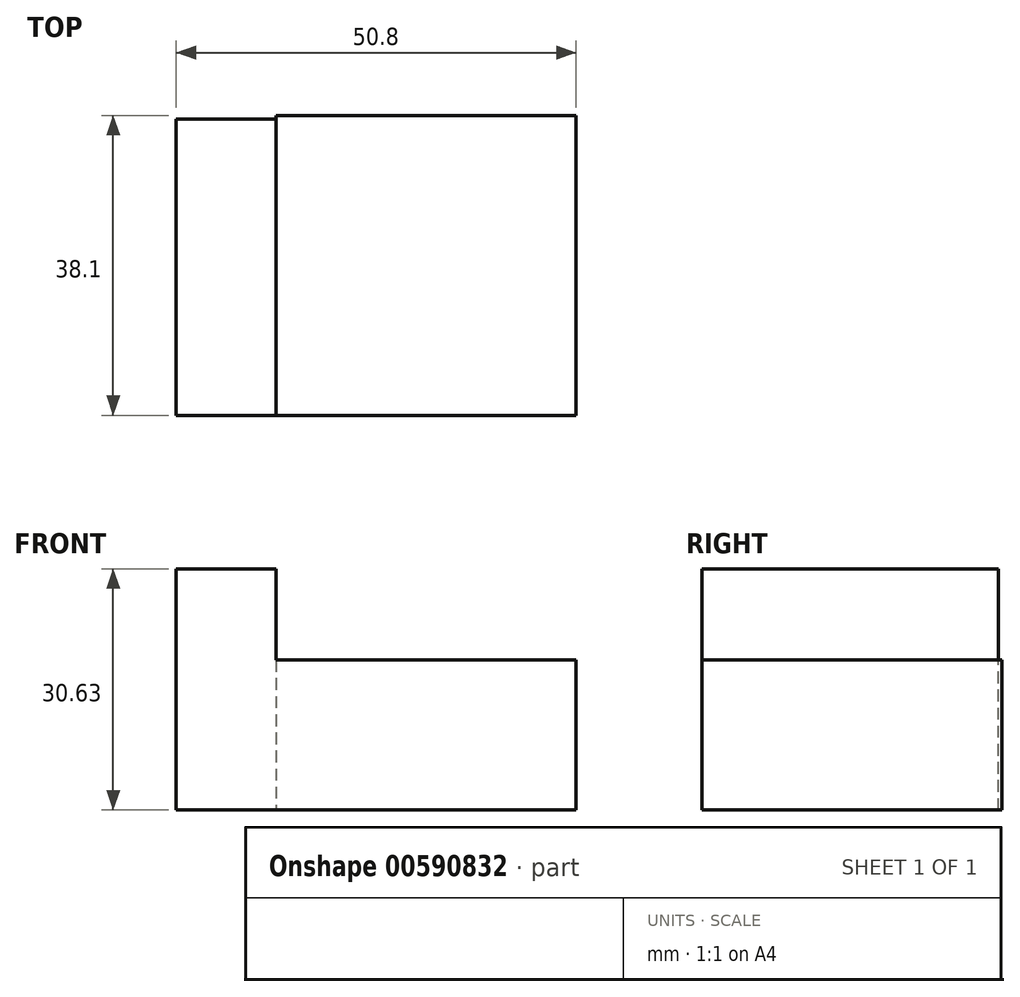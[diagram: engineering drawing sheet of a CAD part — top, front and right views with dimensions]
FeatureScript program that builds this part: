
annotation { "Feature Type Name" : "Feature", "Feature Type Description" : "" }
export const myFeature = defineFeature(function(context is Context, id is Id, definition is map)
    precondition{}
    {
        {
            var Q0;
            Q0=qCreatedBy(makeId("Top.planeOp"),FACE);
            var sketch = newSketch(context, id + "F0", { "sketchPlane" : qUnion([Q0])});
            skLineSegment(sketch, "E0", {"start": v(-21.24, 17.91) * mm, "end": v(-21.24, -20.19) * mm});
            skLineSegment(sketch, "E1", {"start": v(-21.24, -20.19) * mm, "end": v(16.86, -20.19) * mm});
            skLineSegment(sketch, "E2", {"start": v(16.86, -20.19) * mm, "end": v(16.86, 17.91) * mm});
            skLineSegment(sketch, "E3", {"start": v(16.86, 17.91) * mm, "end": v(-21.24, 17.91) * mm});
            skSolve(sketch);
        }
        {
            var Q0;
            Q0=makeQuery(id+"F0.imprint","IMPRINT",FACE,{"disambiguationData":[TD([[makeQuery(id+"F0.imprint","IMPRINT",EDGE,{"derivedFrom":sQuery(id+"F0.wireOp",EDGE,"E0")}),1.0]])]});
            extrude(context, id + "F1", {"entities" : qUnion([Q0]), "depth" : 19.05 * mm, "offsetDistance" : 25.4 * mm});
        }
        {
            var Q0;
            Q0=makeQuery(id+"F1.opExtrude","SWEPT_FACE",FACE,{"disambiguationData":[OSD([sQuery(id+"F0.wireOp",EDGE,"E0")])]});
            var sketch = newSketch(context, id + "F2", { "sketchPlane" : qUnion([Q0])});
            skLineSegment(sketch, "E4", {"start": v(20.19, 2.7) * mm, "end": v(20.19, 30.63) * mm});
            skLineSegment(sketch, "E5", {"start": v(20.19, 30.63) * mm, "end": v(-17.46, 30.63) * mm});
            skLineSegment(sketch, "E6", {"start": v(-17.46, 30.63) * mm, "end": v(-17.45, 2.7) * mm});
            skLineSegment(sketch, "E7", {"start": v(-17.45, 2.7) * mm, "end": v(20.19, 2.7) * mm});
            skSolve(sketch);
        }
        {
            var Q0;
            {var subQ3=sQuery(id+"F2.wireOp",EDGE,"E5");Q0=makeQuery(id+"F2.imprint","IMPRINT",FACE,{"disambiguationData":[TD([[makeQuery(id+"F2.imprint","IMPRINT",EDGE,{"derivedFrom":subQ3}),1.0]])]});}
            extrude(context, id + "F3", {"entities" : qUnion([Q0]), "depth" : 12.7 * mm, "offsetDistance" : 25.4 * mm});
        }
        {
            var Q0;
            Q0=makeQuery(id+"F3.opExtrude","SWEPT_FACE",FACE,{"disambiguationData":[OSD([sQuery(id+"F0.wireOp",EDGE,"E0")])]});
            extrude(context, id + "F4", {"entities" : qUnion([Q0]), "operationType" : NewBodyOperationType.ADD, "depth" : 19.05 * mm, "offsetDistance" : 25.4 * mm});
        }
    });
